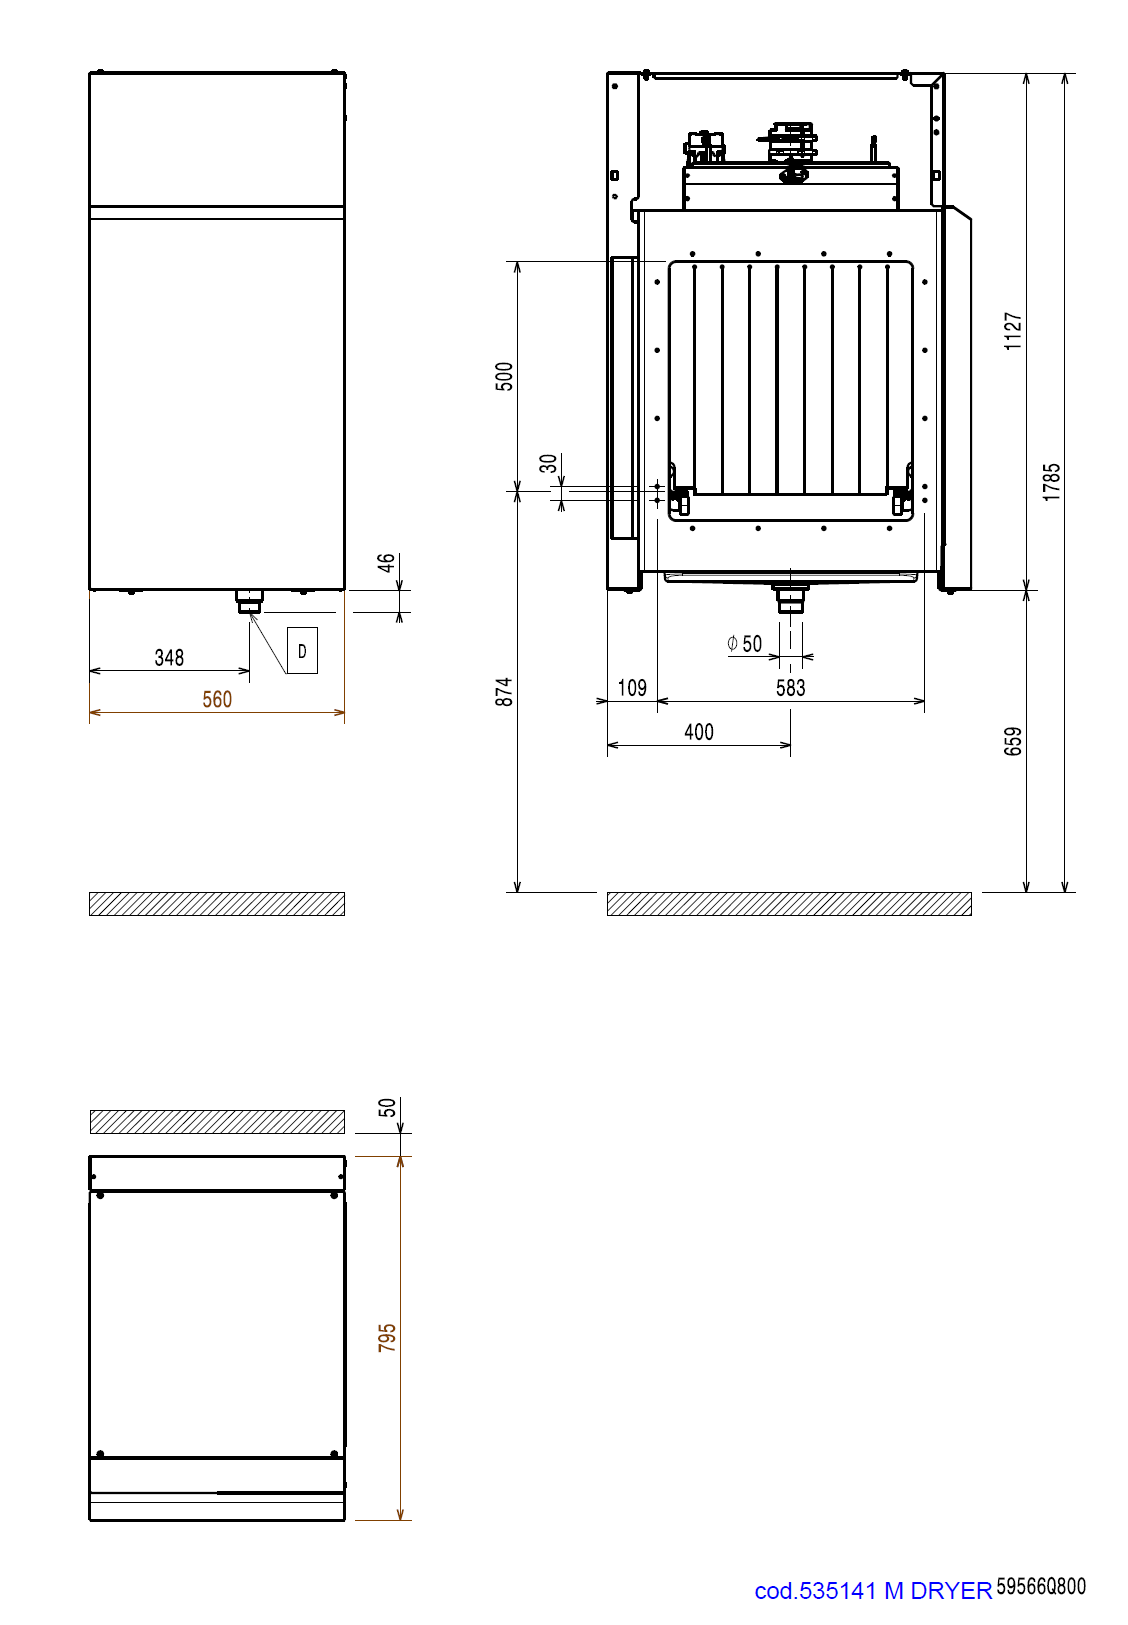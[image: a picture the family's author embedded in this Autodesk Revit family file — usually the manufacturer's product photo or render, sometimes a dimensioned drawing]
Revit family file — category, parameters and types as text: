
# Revit family: QF_ELECTROLUXPROFESSIONAL_535138_NMHABDR6M
name_source: partatom
category: Specialty Equipment
revit_build: Autodesk Revit 2018 (Build: 20190510_1515(x64)
units: mm (PartAtom-declared; Revit-internal decimal feet)

## family parameters
Always vertical = Yes
Cut with Voids When Loaded = No
Part Type = Normal
Room Calculation Point = No
Round Connector Dimension = Use Diameter
Shared = No
Work Plane-Based = No

## types (2) — shared parameters
Accessory = Yes
Cold Water Size = 0 mm
Compressed Air Pressure = 0.0 Pa
Compressed Air Size = 0 mm
Compressed Air Volume = 0.0 L/s
Condensate Return Size = 0 mm
Depth Actual = 795 mm  [stored 2.60827 ft]
Direct Waste Size = 50 mm
Gas Input Pressure = 0
Gas Size = 0 mm
HP = 5.9 HP
Height Actual = 1130 mm  [stored 3.70735 ft]
Hot Water Size = 0 mm
Length Actual = 560 mm  [stored 1.83727 ft]
Refrigerant Compressor Remote = Yes
Refrigeration Liquid Line Size = 0 mm
Refrigeration Suction Line Size = 0 mm
Steam Supply Maximum Pressure = 0.0 Pa
Steam Supply Minimum Pressure = 0.0 Pa
Steam Supply Size = 0 mm
URL = http://professional.electrolux.com
Watts = 0 W
Weight = 0.00 kg
zero-valued in all types: Gas KW, Steam Pounds per Hour

## per-type parameters (varying)
| type | Cycle | Description | Item Number | Manufacturer | Model | Phase | URL Manufacturer | Volts |
| NMHDRE56 | 0 Hz | SINGLE RINSE RT, 100R/H, ELECTRIC 50HZ |  | Electrolux | ESR10E5 | 0 |  | 0 V |
| Standard | 60 Hz | MEDIUM DRYER WITHOUT DOOR (HAB), DUAL RINSE RT, ELECTRIC, 440/ 3/ 60Hz-MARINE | 535138 | Electrolux Professional | NMHABDR6M | 3 | http://professional.electrolux.com | 400 V |

note: source unit labels omitted for Gas Input Pressure — the stored unit's dimension contradicts the parameter name (converter mislabeling)

note: [stored X ft] marks values corroborated as IEEE doubles in the binary element streams (Revit-internal decimal feet)
